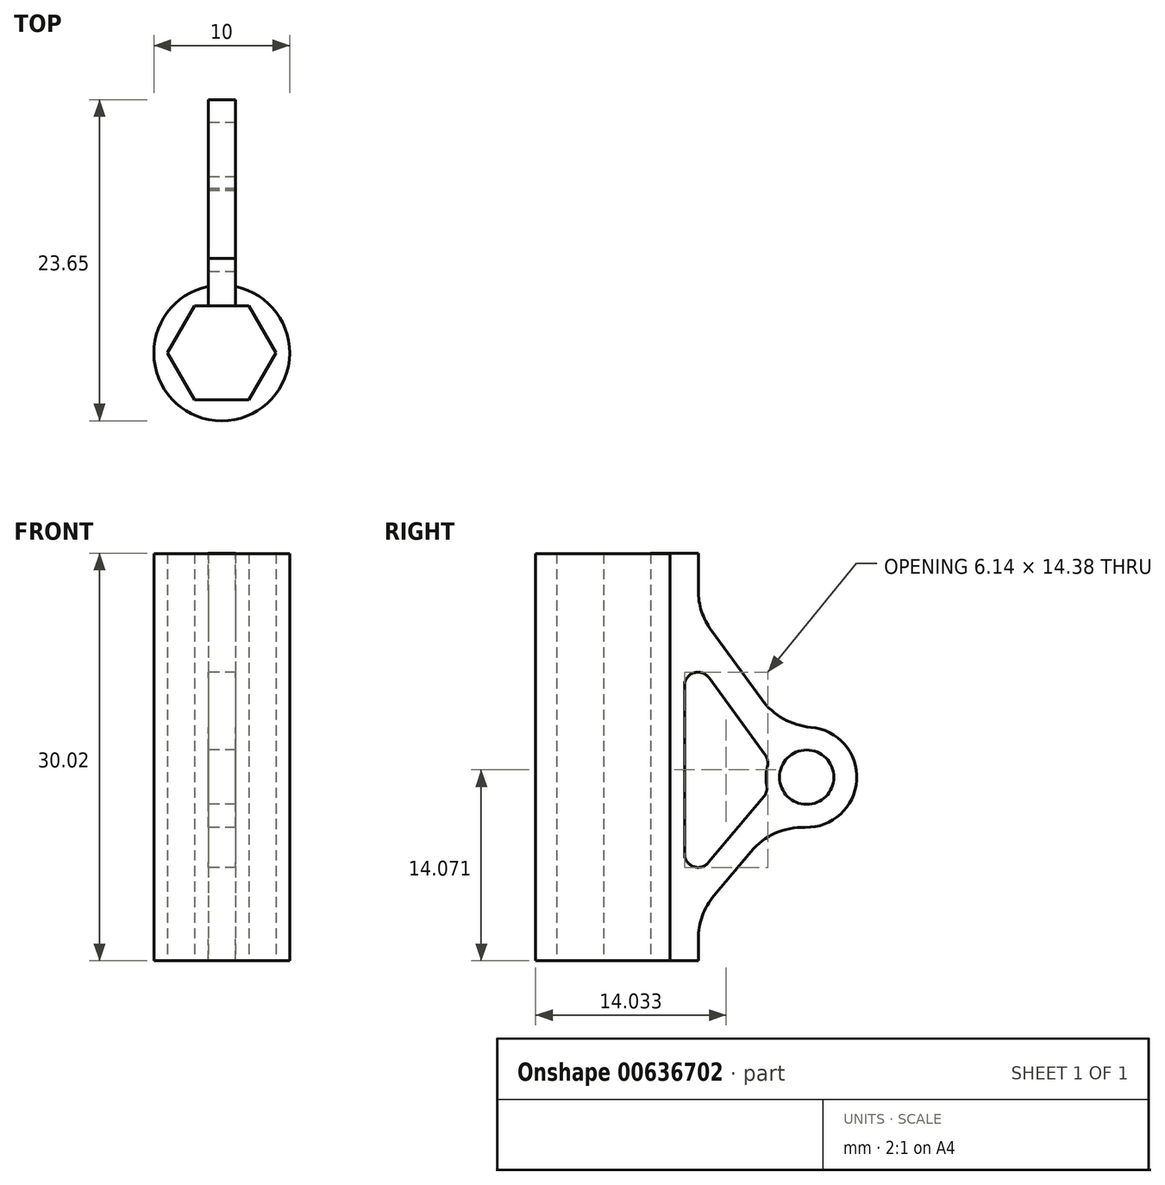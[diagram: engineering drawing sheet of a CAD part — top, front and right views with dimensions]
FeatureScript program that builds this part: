
annotation { "Feature Type Name" : "Feature", "Feature Type Description" : "" }
export const myFeature = defineFeature(function(context is Context, id is Id, definition is map)
    precondition{}
    {
        {
            var Q0;
            Q0=qCreatedBy(makeId("Right.planeOp"),FACE);
            var sketch = newSketch(context, id + "F0", { "sketchPlane" : qUnion([Q0])});
            skLineSegment(sketch, "E0", {"start": v(-38.1, 26.48) * mm, "end": v(-38.1, -3.54) * mm});
            skCircle(sketch, "E1", {"center": v(-26.6, 9.98) * mm, "radius": 2 * mm});
            skArc(sketch, "E2", {"start": v(-29.5, 10.77) * mm, "mid": v(-29.6, 10.09) * mm, "end": v(-29.55, 9.4) * mm});
            skLineSegment(sketch, "E3.0", {"start": v(-33.8, 17.3) * mm, "end": v(-29.66, 11.62) * mm});
            skLineSegment(sketch, "E3.1", {"start": v(-35.6, 16.72) * mm, "end": v(-35.6, 4.34) * mm});
            skLineSegment(sketch, "E3.2", {"start": v(-29.76, 8.56) * mm, "end": v(-33.84, 3.7) * mm});
            skLineSegment(sketch, "E4.2", {"start": v(-30.7, 4.51) * mm, "end": v(-31.4, 3.69) * mm});
            skLineSegment(sketch, "E5.0", {"start": v(-33.63, 20.8) * mm, "end": v(-29.92, 15.7) * mm});
            skPoint(sketch, "E6.visualSharp", {"position": v(-35.6, 19.79) * mm});
            skArc(sketch, "E6.filletArc", {"start": v(-33.8, 17.3) * mm, "mid": v(-34.92, 17.67) * mm, "end": v(-35.6, 16.72) * mm});
            skPoint(sketch, "E7.visualSharp", {"position": v(-35.6, 1.6) * mm});
            skArc(sketch, "E7.filletArc", {"start": v(-35.6, 4.34) * mm, "mid": v(-34.95, 3.4) * mm, "end": v(-33.84, 3.7) * mm});
            skPoint(sketch, "E8.visualSharp", {"position": v(-35.75, 23.7) * mm});
            skPoint(sketch, "E9.visualSharp", {"position": v(-29.43, 8.96) * mm});
            skArc(sketch, "E9.filletArc", {"start": v(-29.76, 8.56) * mm, "mid": v(-29.56, 8.95) * mm, "end": v(-29.55, 9.4) * mm});
            skPoint(sketch, "E10.visualSharp", {"position": v(-29.35, 11.2) * mm});
            skArc(sketch, "E10.filletArc", {"start": v(-29.5, 10.77) * mm, "mid": v(-29.48, 11.22) * mm, "end": v(-29.66, 11.62) * mm});
            skLineSegment(sketch, "E11", {"start": v(-38.1, 26.48) * mm, "end": v(-34.6, 26.48) * mm});
            skLineSegment(sketch, "E12", {"start": v(-34.6, 23.75) * mm, "end": v(-34.6, 26.48) * mm});
            skLineSegment(sketch, "E13", {"start": v(-38.1, -3.54) * mm, "end": v(-34.6, -3.54) * mm});
            skLineSegment(sketch, "E14", {"start": v(-31.4, 3.69) * mm, "end": v(-33.42, 1.27) * mm});
            skLineSegment(sketch, "E15", {"start": v(-34.6, -3.54) * mm, "end": v(-34.6, -1.94) * mm});
            skPoint(sketch, "E16.visualSharp", {"position": v(-34.6, 22.12) * mm});
            skArc(sketch, "E16.filletArc", {"start": v(-34.6, 23.75) * mm, "mid": v(-34.35, 22.2) * mm, "end": v(-33.63, 20.8) * mm});
            skPoint(sketch, "E17.visualSharp", {"position": v(-34.6, -0.12) * mm});
            skArc(sketch, "E17.filletArc", {"start": v(-33.42, 1.27) * mm, "mid": v(-34.3, -0.23) * mm, "end": v(-34.6, -1.94) * mm});
            skArc(sketch, "E18", {"start": v(-26.72, 6.3) * mm, "mid": v(-22.92, 9.77) * mm, "end": v(-26.3, 13.66) * mm});
            skPoint(sketch, "E19.visualSharp", {"position": v(-28.67, 6.93) * mm});
            skArc(sketch, "E19.filletArc", {"start": v(-26.72, 6.3) * mm, "mid": v(-28.91, 5.86) * mm, "end": v(-30.7, 4.51) * mm});
            skPoint(sketch, "E20.visualSharp", {"position": v(-28.18, 13.32) * mm});
            skArc(sketch, "E20.filletArc", {"start": v(-29.92, 15.7) * mm, "mid": v(-28.33, 14.29) * mm, "end": v(-26.3, 13.66) * mm});
            skSolve(sketch);
        }
        {
            var Q0;
            Q0=makeQuery(id+"F0.imprint","IMPRINT",FACE,{"disambiguationData":[TD([[makeQuery(id+"F0.imprint","IMPRINT",EDGE,{"derivedFrom":sQuery(id+"F0.wireOp",EDGE,"E0")}),1.0]])]});
            extrude(context, id + "F1", {"entities" : qUnion([Q0]), "depth" : 2 * mm, "offsetDistance" : 25 * mm});
        }
        {
            var Q0;
            Q0=makeQuery(id+"F1.opExtrude","SWEPT_FACE",FACE,{"disambiguationData":[OSD([sQuery(id+"F0.wireOp",EDGE,"E13")])]});
            var sketch = newSketch(context, id + "F2", { "sketchPlane" : qUnion([Q0])});
            skCircle(sketch, "E21.cCircle", {"center": v(1, 41.57) * mm, "radius": 3.46 * mm, "construction": true});
            skLineSegment(sketch, "E21.0", {"start": v(3, 45.04) * mm, "end": v(5, 41.57) * mm});
            skLineSegment(sketch, "E21.1", {"start": v(5, 41.57) * mm, "end": v(3, 38.1) * mm});
            skLineSegment(sketch, "E21.2", {"start": v(3, 38.1) * mm, "end": v(-1, 38.1) * mm});
            skLineSegment(sketch, "E21.3", {"start": v(-1, 38.1) * mm, "end": v(-3, 41.57) * mm});
            skLineSegment(sketch, "E21.4", {"start": v(-3, 41.57) * mm, "end": v(-1, 45.03) * mm});
            skLineSegment(sketch, "E21.5", {"start": v(-1, 45.03) * mm, "end": v(3, 45.04) * mm});
            skPoint(sketch, "E21.0.midPoint", {"position": v(4, 43.3) * mm});
            skCircle(sketch, "E22", {"center": v(1, 41.57) * mm, "radius": 5 * mm});
            skSolve(sketch);
        }
        {
            var Q0;
            {var subQ0=sQuery(id+"F2.wireOp",EDGE,"E21.2");var subQ1=sQuery(id+"F0.wireOp",EDGE,"E13");var subQ2=makeQuery(id+"F1.opExtrude","CAP_EDGE",EDGE,{"disambiguationData":[OSD([subQ1])],"isStart":false});var subQ3=makeQuery(id+"F2.imprint","INTERSECT",VERTEX,{"derivedFrom":[subQ2,subQ0]});Q0=makeQuery(id+"F2.imprint","IMPRINT",FACE,{"disambiguationData":[TD([[makeQuery(id+"F2.imprint","IMPRINT",EDGE,{"disambiguationData":[TD([[subQ3,-1.0]])],"derivedFrom":subQ0}),1.0]])]});}
            var Q1;
            Q1=makeQuery(id+"F2.imprint","IMPRINT",FACE,{"disambiguationData":[TD([[makeQuery(id+"F2.imprint","IMPRINT",EDGE,{"derivedFrom":sQuery(id+"F2.wireOp",EDGE,"E21.0")}),1.0]])]});
            extrude(context, id + "F3", {"entities" : qUnion([Q0, Q1]), "operationType" : NewBodyOperationType.ADD, "oppositeDirection" : true, "depth" : 30 * mm, "offsetDistance" : 25 * mm});
        }
    });
